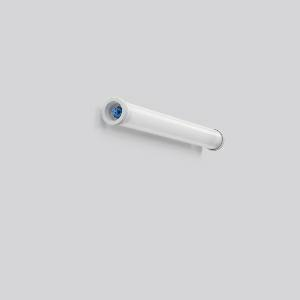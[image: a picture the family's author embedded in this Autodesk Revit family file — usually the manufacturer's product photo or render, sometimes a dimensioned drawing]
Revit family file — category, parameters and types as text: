
# Revit family: planox_tube_601070_002_eb3c
name_source: partatom
category: Lighting Fixtures
units: mm (PartAtom-declared; Revit-internal decimal feet)

## family parameters
Cut with Voids When Loaded = No
Host = Face
Light Source = No
Part Type = Normal
Room Calculation Point = No
Round Connector Dimension = Use Diameter
Shared = No

## types (1)
- PLANOX TUBE (1 x LED Modul 840, 3500 lm, 4000)
    Apparent Load = 31 VA
    CIE Flux Codes = 41 70 89 89 100
    Color Rendering = 80
    Color Temperature = 4000
    Default Elevation = 1800 mm
    Description = Series: PLANOX TUBE
Robust protective tube luminaire for tough requirements. Rack made of sheet steel, white powder coated. End caps made of plastic (polyamide) grey. Diffuser made of plastic (polycarbonate), opal, shockproof. Symmetrical light distribution. Homogeneous light distribution. With accessories for wall, ceiling or pendant mounting. Driver integrated.Easy installation with the Plug+Play Wieland RST CLASSIC plug-in system. Mounting set must be ordered separately. Luminaire with limited surface temperature in accordance with EN 60598-2-24 for use in environments in which a deposit of conductive dust on the luminaire can be expected. Qualified for use in the food and drink industry. Suitable for lighting in public car parks and public off-street parking spaces according to DIN 67528. Environmentally friendly and resource-saving due to replaceable components. 
Colour: white
Diameter: 78 mm
Length: 722 mm
Lamp: LED
Socket: without socket
Colour temperature: 4000K
Colour rendering index (CRI): 83
System power: 31 W
Rated luminous flux: 3500 lm
Luminous efficiency: 113 lm/W
Control gear: Regulated power supply
Protection class: I
Type of protection: IP 67
    Height = 0 mm  [stored 0 ft]
    Lamp = 1 x LED Modul 840
    Lamp Light Flux = 3500 lm
    Lamp count = 1
    Length = 722 mm
    Lifetime = 50000 h
    Luminous efficacy = 113 lm/W
    Manufacturer = RZB
    ModVariant = No
    Model = 601070.002
    Mounting Place = Ceiling
    Mounting Type = Surface mounted
    Number of Poles = 1
    OnlyDefault = Yes
    Power Factor = 1
    Product Name = PLANOX TUBE
    Product group = Surface mounted luminaires for moist/humid enviroments
    ProductGroupID = 308
    Protection Class = Protection class I
    Protection Degree = Degree of protection
    RLX_Detail_Level = 1
    RLX_Emergency_Light_Flux = 0 lm
    RLX_Emergency_Type = 0
    RLX_Emergency_Type_DB = No
    RlxData = <blob elided: 31721 chars, md5=64415bb2>
    Socket = socket
    Standby Power = 0 W
    System Light Flux = 3500 lm
    System Power = 31 W
    Type Comments = Product without accessories
    Type Image = 601070.002.jpg
    URL = http://relux.com
    VarID = ---
    Voltage = 0 V
    Weight = 0.00 kg
    Width = 0 mm  [stored 0 ft]

note: [stored X ft] marks values corroborated as IEEE doubles in the binary element streams (Revit-internal decimal feet)

## geometry (parser evidence)
native form markers: Blend x4, Sweep x11
no freeform markers — native parametric forms only
